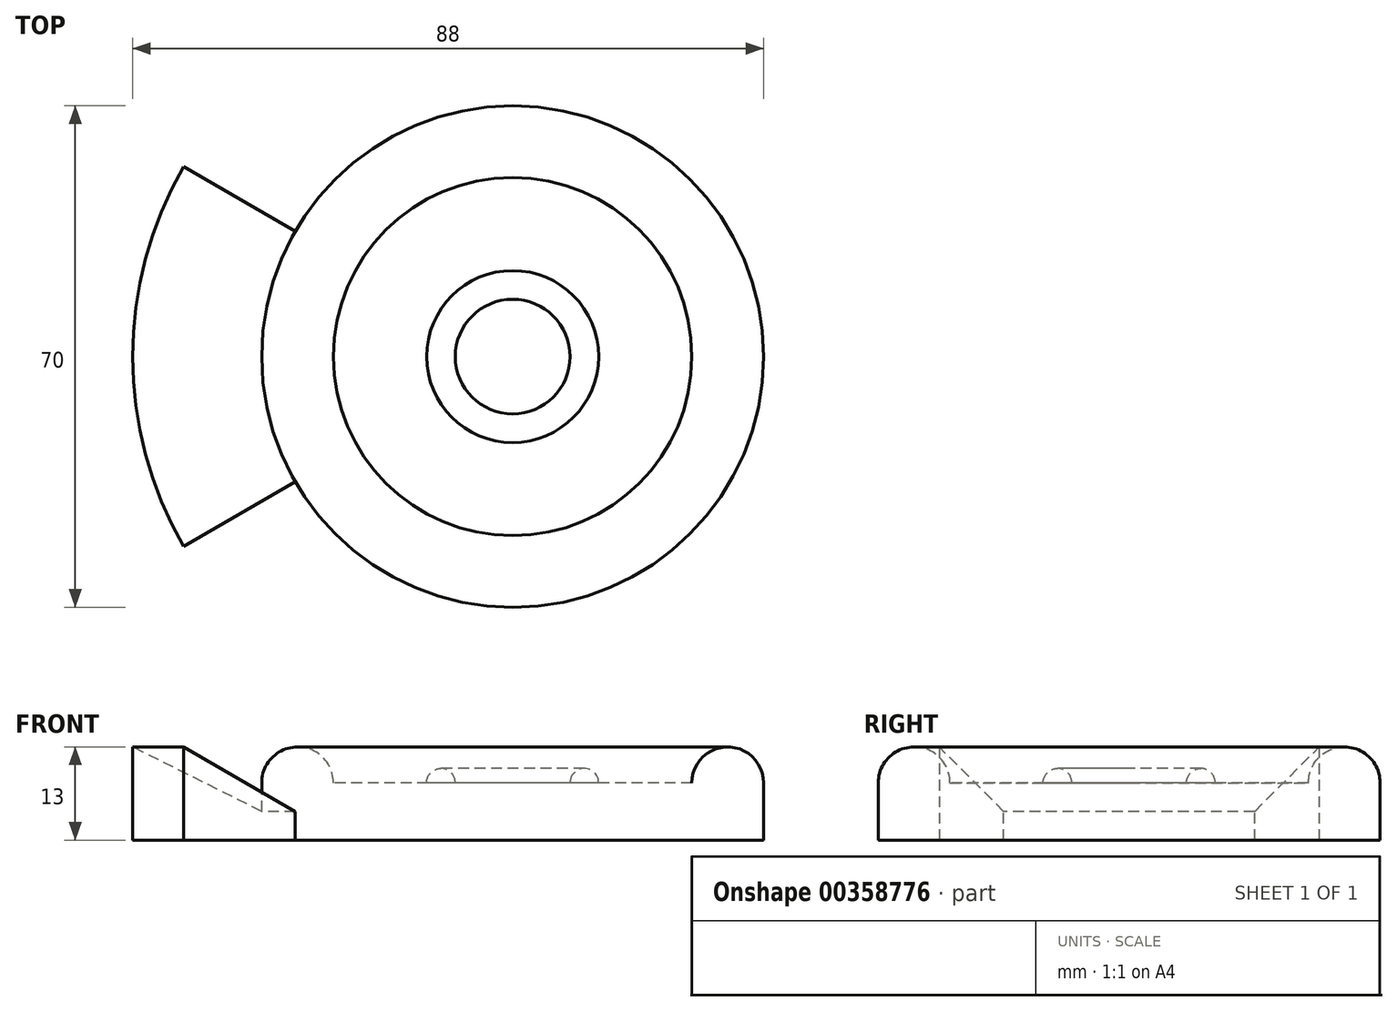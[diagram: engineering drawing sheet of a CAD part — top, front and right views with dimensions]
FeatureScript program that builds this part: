
annotation { "Feature Type Name" : "Feature", "Feature Type Description" : "" }
export const myFeature = defineFeature(function(context is Context, id is Id, definition is map)
    precondition{}
    {
        {
            var Q0;
            Q0=qCreatedBy(makeId("Front.planeOp"),FACE);
            var sketch = newSketch(context, id + "F0", { "sketchPlane" : qUnion([Q0])});
            skLineSegment(sketch, "E0", {"start": v(0, 0) * mm, "end": v(0, -8) * mm});
            skLineSegment(sketch, "E1", {"start": v(0, -8) * mm, "end": v(-35, -8) * mm});
            skLineSegment(sketch, "E2", {"start": v(-35, -8) * mm, "end": v(-35, 0) * mm});
            skLineSegment(sketch, "E3", {"start": v(-25, 0) * mm, "end": v(0, 0) * mm});
            skLineSegment(sketch, "E4", {"start": v(-35, -8) * mm, "end": v(-53, -8) * mm});
            skLineSegment(sketch, "E5", {"start": v(-35, -4) * mm, "end": v(-53, 5) * mm});
            skLineSegment(sketch, "E6", {"start": v(-53, 5) * mm, "end": v(-53, -8) * mm});
            skArc(sketch, "E7", {"start": v(-25, 0) * mm, "mid": v(-30, 5) * mm, "end": v(-35, 0) * mm});
            skArc(sketch, "E8", {"start": v(-8, 0) * mm, "mid": v(-10, 2) * mm, "end": v(-12, 0) * mm});
            skSolve(sketch);
        }
        {
            var Q0;
            Q0=makeQuery(id+"F0.imprint","IMPRINT",FACE,{"disambiguationData":[TD([[makeQuery(id+"F0.imprint","IMPRINT",EDGE,{"derivedFrom":sQuery(id+"F0.wireOp",EDGE,"E0")}),-1.0]])]});
            var Q1;
            {var subQ0=sQuery(id+"F0.wireOp",EDGE,"E8");Q1=makeQuery(id+"F0.imprint","IMPRINT",FACE,{"disambiguationData":[TD([[makeQuery(id+"F0.imprint","IMPRINT",EDGE,{"derivedFrom":subQ0}),1.0]])]});}
            var Q2;
            Q2=sQuery(id+"F0.wireOp",EDGE,"E0");
            revolve(context, id + "F1", {"entities" : qUnion([Q0, Q1]), "axis" : qUnion([Q2]), "revolveType" : RevolveType.FULL});
        }
        {
            var Q0;
            {var subQ0=sQuery(id+"F0.wireOp",EDGE,"E4");Q0=makeQuery(id+"F0.imprint","IMPRINT",FACE,{"disambiguationData":[TD([[makeQuery(id+"F0.imprint","IMPRINT",EDGE,{"derivedFrom":subQ0}),-1.0]])]});}
            var Q1;
            Q1=sQuery(id+"F0.wireOp",EDGE,"E0");
            revolve(context, id + "F2", {"operationType" : NewBodyOperationType.ADD, "entities" : qUnion([Q0]), "axis" : qUnion([Q1]), "revolveType" : RevolveType.SYMMETRIC, "angle" : 60 * degree});
        }
    });
